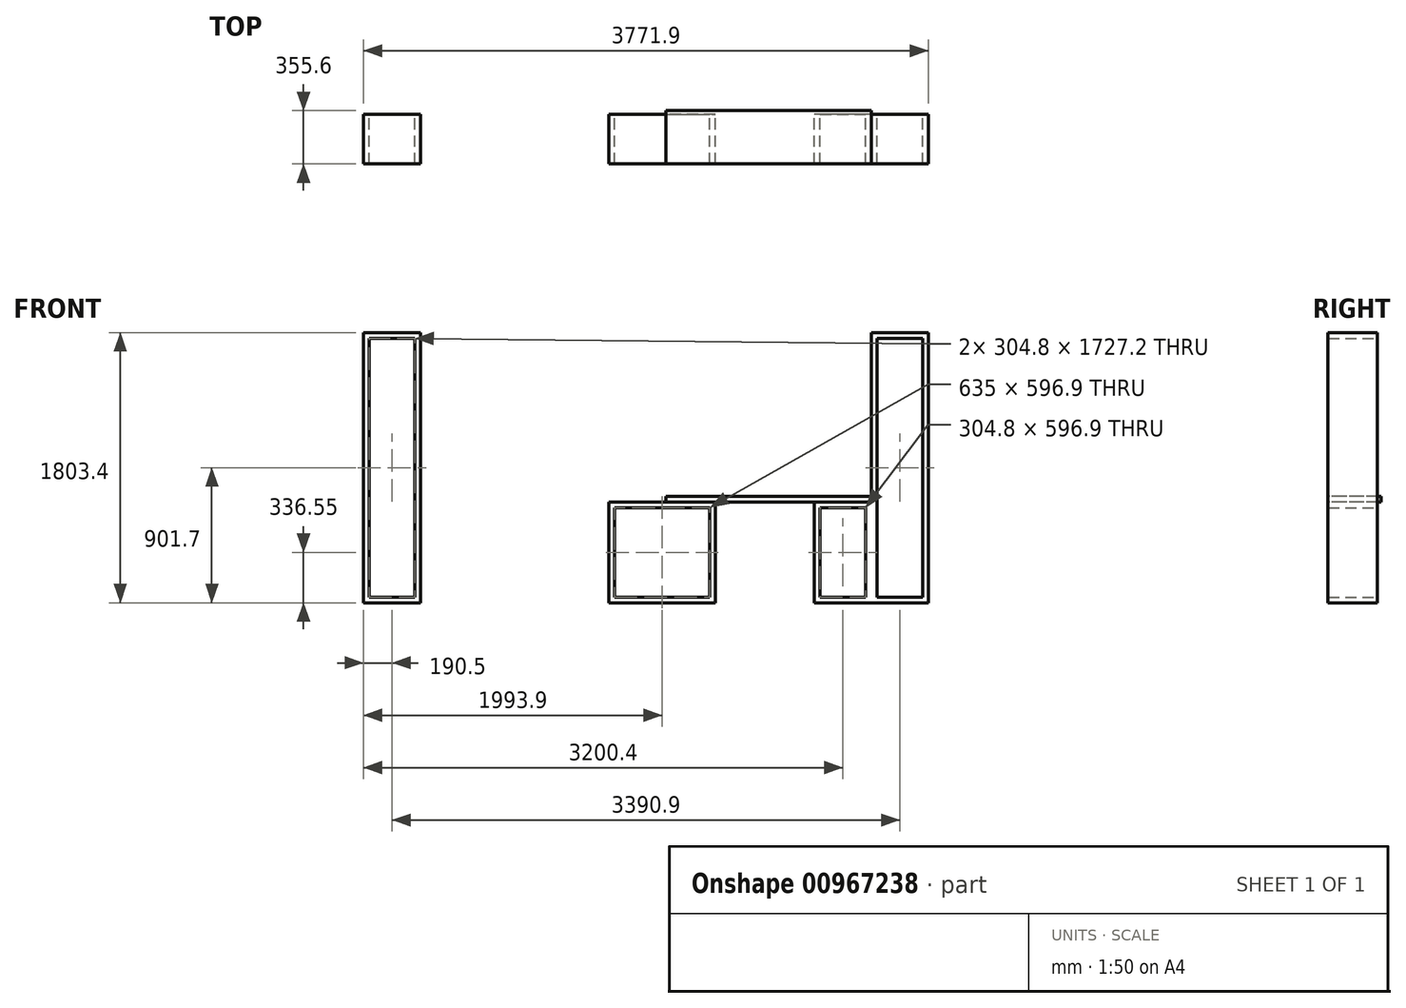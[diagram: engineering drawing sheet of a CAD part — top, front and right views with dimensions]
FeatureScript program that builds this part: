
annotation { "Feature Type Name" : "Feature", "Feature Type Description" : "" }
export const myFeature = defineFeature(function(context is Context, id is Id, definition is map)
    precondition{}
    {
        {
            var Q0;
            Q0=qCreatedBy(makeId("Front.planeOp"),FACE);
            var sketch = newSketch(context, id + "F0", { "sketchPlane" : qUnion([Q0])});
            skLineSegment(sketch, "E0.bottom", {"start": v(0, 0) * mm, "end": v(-38.1, 0) * mm});
            skLineSegment(sketch, "E0.top", {"start": v(0, 1803.4) * mm, "end": v(-38.1, 1803.4) * mm});
            skLineSegment(sketch, "E0.left", {"start": v(0, 0) * mm, "end": v(0, 1803.4) * mm});
            skLineSegment(sketch, "E0.right", {"start": v(-38.1, 38.1) * mm, "end": v(-38.1, 1765.3) * mm});
            skLineSegment(sketch, "E1.bottom", {"start": v(-38.1, 0) * mm, "end": v(-342.9, 0) * mm});
            skLineSegment(sketch, "E1.top", {"start": v(-38.1, 38.1) * mm, "end": v(-342.9, 38.1) * mm});
            skLineSegment(sketch, "E2", {"start": v(-38.1, 1803.4) * mm, "end": v(-4282.89, 1803.4) * mm, "construction": true});
            skLineSegment(sketch, "E3", {"start": v(0, 711.2) * mm, "end": v(-3409.65, 711.2) * mm, "construction": true});
            skLineSegment(sketch, "E4", {"start": v(-3771.9, 1803.4) * mm, "end": v(-3771.9, 0) * mm, "construction": true});
            skLineSegment(sketch, "E5.bottom", {"start": v(-342.9, 0) * mm, "end": v(-381, 0) * mm});
            skLineSegment(sketch, "E5.top", {"start": v(-342.9, 1803.4) * mm, "end": v(-381, 1803.4) * mm});
            skLineSegment(sketch, "E5.left", {"start": v(-342.9, 38.1) * mm, "end": v(-342.9, 1765.3) * mm});
            skLineSegment(sketch, "E5.right", {"start": v(-381, 0) * mm, "end": v(-381, 1803.4) * mm});
            skLineSegment(sketch, "E6.bottom", {"start": v(-342.9, 1803.4) * mm, "end": v(-38.1, 1803.4) * mm});
            skLineSegment(sketch, "E6.top", {"start": v(-342.9, 1765.3) * mm, "end": v(-38.1, 1765.3) * mm});
            skLineSegment(sketch, "E7.top", {"start": v(-1752.6, 1803.4) * mm, "end": v(-2133.6, 1803.4) * mm});
            skLineSegment(sketch, "E7.left", {"start": v(-1752.6, 711.2) * mm, "end": v(-1752.6, 1803.4) * mm});
            skLineSegment(sketch, "E7.right", {"start": v(-2133.6, 0) * mm, "end": v(-2133.6, 673.1) * mm});
            skLineSegment(sketch, "E8.top", {"start": v(-2095.5, 1765.3) * mm, "end": v(-1790.7, 1765.3) * mm});
            skLineSegment(sketch, "E8.left", {"start": v(-2095.5, 38.1) * mm, "end": v(-2095.5, 673.1) * mm});
            skLineSegment(sketch, "E8.right", {"start": v(-1790.7, 711.2) * mm, "end": v(-1790.7, 1765.3) * mm});
            skLineSegment(sketch, "E9.bottom", {"start": v(-381, 673.1) * mm, "end": v(-762, 673.1) * mm});
            skLineSegment(sketch, "E9.top", {"start": v(-381, 0) * mm, "end": v(-762, 0) * mm});
            skLineSegment(sketch, "E9.left", {"start": v(-381, 673.1) * mm, "end": v(-381, 0) * mm});
            skLineSegment(sketch, "E9.right", {"start": v(-762, 673.1) * mm, "end": v(-762, 0) * mm});
            skLineSegment(sketch, "E10.bottom", {"start": v(-723.9, 635) * mm, "end": v(-419.1, 635) * mm});
            skLineSegment(sketch, "E10.top", {"start": v(-723.9, 38.1) * mm, "end": v(-419.1, 38.1) * mm});
            skLineSegment(sketch, "E10.left", {"start": v(-723.9, 635) * mm, "end": v(-723.9, 38.1) * mm});
            skLineSegment(sketch, "E10.right", {"start": v(-419.1, 635) * mm, "end": v(-419.1, 38.1) * mm});
            skLineSegment(sketch, "E11.bottom", {"start": v(-1752.6, 0) * mm, "end": v(-1422.4, 0) * mm});
            skLineSegment(sketch, "E11.right", {"start": v(-1422.4, 0) * mm, "end": v(-1422.4, 673.1) * mm});
            skLineSegment(sketch, "E12", {"start": v(-1422.4, 673.1) * mm, "end": v(-762, 673.1) * mm, "construction": true});
            skLineSegment(sketch, "E13.bottom", {"start": v(-3771.9, 0) * mm, "end": v(-3390.9, 0) * mm});
            skLineSegment(sketch, "E13.top", {"start": v(-3771.9, 1803.4) * mm, "end": v(-3390.9, 1803.4) * mm});
            skLineSegment(sketch, "E13.left", {"start": v(-3771.9, 0) * mm, "end": v(-3771.9, 1803.4) * mm});
            skLineSegment(sketch, "E13.right", {"start": v(-3390.9, 0) * mm, "end": v(-3390.9, 1803.4) * mm});
            skLineSegment(sketch, "E14.bottom", {"start": v(-3733.8, 1765.3) * mm, "end": v(-3429, 1765.3) * mm});
            skLineSegment(sketch, "E14.top", {"start": v(-3733.8, 38.1) * mm, "end": v(-3429, 38.1) * mm});
            skLineSegment(sketch, "E14.left", {"start": v(-3733.8, 1765.3) * mm, "end": v(-3733.8, 38.1) * mm});
            skLineSegment(sketch, "E14.right", {"start": v(-3429, 1765.3) * mm, "end": v(-3429, 38.1) * mm});
            skLineSegment(sketch, "E15", {"start": v(-1752.6, 673.1) * mm, "end": v(-1790.7, 673.1) * mm});
            skPoint(sketch, "E16.endSnap0", {"position": v(-1166.41, 1228.6) * mm});
            skPoint(sketch, "E16.end.orphan", {"position": v(-1166.41, 1373.93) * mm});
            skLineSegment(sketch, "E17", {"start": v(-1422.4, 673.1) * mm, "end": v(-1752.6, 673.1) * mm});
            skLineSegment(sketch, "E18", {"start": v(-2133.6, 0) * mm, "end": v(-1752.6, 0) * mm});
            skPoint(sketch, "E19.orphan", {"position": v(-1166.41, 1285.9) * mm});
            skPoint(sketch, "E20.start.orphan", {"position": v(-1166.41, 1171.28) * mm});
            skLineSegment(sketch, "E21", {"start": v(-2095.5, 38.1) * mm, "end": v(-1460.5, 38.1) * mm});
            skLineSegment(sketch, "E22", {"start": v(-1460.5, 38.1) * mm, "end": v(-1460.5, 635) * mm});
            skLineSegment(sketch, "E23", {"start": v(-1460.5, 635) * mm, "end": v(-2095.5, 635) * mm});
            skLineSegment(sketch, "E24", {"start": v(-1790.7, 673.1) * mm, "end": v(-2133.6, 673.1) * mm});
            skLineSegment(sketch, "E25", {"start": v(-2133.6, 711.2) * mm, "end": v(-1752.6, 711.2) * mm});
            skLineSegment(sketch, "E26.trimOffspring", {"start": v(-2095.5, 711.2) * mm, "end": v(-2095.5, 1765.3) * mm});
            skLineSegment(sketch, "E27.trimOffspring", {"start": v(-2133.6, 711.2) * mm, "end": v(-2133.6, 1803.4) * mm});
            skSolve(sketch);
        }
        {
            var Q0;
            Q0=makeQuery(id+"F0.imprint","IMPRINT",FACE,{"disambiguationData":[TD([[makeQuery(id+"F0.imprint","IMPRINT",EDGE,{"derivedFrom":sQuery(id+"F0.wireOp",EDGE,"E13.bottom")}),1.0]])]});
            var Q1;
            Q1=makeQuery(id+"F0.imprint","IMPRINT",FACE,{"disambiguationData":[TD([[makeQuery(id+"F0.imprint","IMPRINT",EDGE,{"derivedFrom":sQuery(id+"F0.wireOp",EDGE,"E7.bottom")}),-1.0]])]});
            var Q2;
            Q2=makeQuery(id+"F0.imprint","IMPRINT",FACE,{"disambiguationData":[TD([[makeQuery(id+"F0.imprint","IMPRINT",EDGE,{"derivedFrom":sQuery(id+"F0.wireOp",EDGE,"E11.bottom")}),1.0]])]});
            var Q3;
            Q3=makeQuery(id+"F0.imprint","IMPRINT",FACE,{"disambiguationData":[TD([[makeQuery(id+"F0.imprint","IMPRINT",EDGE,{"derivedFrom":sQuery(id+"F0.wireOp",EDGE,"E9.bottom")}),1.0]])]});
            var Q4;
            Q4=makeQuery(id+"F0.imprint","IMPRINT",FACE,{"disambiguationData":[TD([[makeQuery(id+"F0.imprint","IMPRINT",EDGE,{"derivedFrom":sQuery(id+"F0.wireOp",EDGE,"E0.bottom")}),-1.0]])]});
            extrude(context, id + "F1", {"entities" : qUnion([Q0, Q1, Q2, Q3, Q4]), "depth" : 330.2 * mm, "offsetDistance" : 25.4 * mm});
        }
        {
            var Q0;
            Q0=makeQuery(id+"F1.opExtrude","CAP_FACE",FACE,{"disambiguationData":[OSD([sQuery(id+"F0.wireOp",EDGE,"E7.bottom"),sQuery(id+"F0.wireOp",EDGE,"E7.top"),sQuery(id+"F0.wireOp",EDGE,"E7.left"),sQuery(id+"F0.wireOp",EDGE,"E7.right"),sQuery(id+"F0.wireOp",EDGE,"E8.bottom"),sQuery(id+"F0.wireOp",EDGE,"E8.top"),sQuery(id+"F0.wireOp",EDGE,"E8.left"),sQuery(id+"F0.wireOp",EDGE,"E8.right"),sQuery(id+"F0.wireOp",EDGE,"E11.bottom"),sQuery(id+"F0.wireOp",EDGE,"E11.top"),sQuery(id+"F0.wireOp",EDGE,"E11.right"),sQuery(id+"F0.wireOp",EDGE,"qYu8XCY6-Zk7Y-VSSy-7GBY-yCQs0snOXPtU.bottom"),sQuery(id+"F0.wireOp",EDGE,"qYu8XCY6-Zk7Y-VSSy-7GBY-yCQs0snOXPtU.top"),sQuery(id+"F0.wireOp",EDGE,"qYu8XCY6-Zk7Y-VSSy-7GBY-yCQs0snOXPtU.left"),sQuery(id+"F0.wireOp",EDGE,"qYu8XCY6-Zk7Y-VSSy-7GBY-yCQs0snOXPtU.right")])],"isStart":false});
            var sketch = newSketch(context, id + "F2", { "sketchPlane" : qUnion([Q0])});
            skLineSegment(sketch, "E28.bottom", {"start": v(-1752.6, 673.1) * mm, "end": v(-381, 673.1) * mm});
            skLineSegment(sketch, "E28.top", {"start": v(-1752.6, 711.2) * mm, "end": v(-381, 711.2) * mm});
            skLineSegment(sketch, "E28.left", {"start": v(-1752.6, 673.1) * mm, "end": v(-1752.6, 711.2) * mm});
            skLineSegment(sketch, "E28.right", {"start": v(-381, 673.1) * mm, "end": v(-381, 711.2) * mm});
            skSolve(sketch);
        }
        {
            var Q0;
            Q0=makeQuery(id+"F2.imprint","IMPRINT",FACE,{"disambiguationData":[TD([[makeQuery(id+"F2.imprint","IMPRINT",EDGE,{"derivedFrom":sQuery(id+"F2.wireOp",EDGE,"E28.top")}),-1.0]])]});
            extrude(context, id + "F3", {"entities" : qUnion([Q0]), "oppositeDirection" : true, "depth" : 355.6 * mm, "offsetDistance" : 25.4 * mm});
        }
    });
